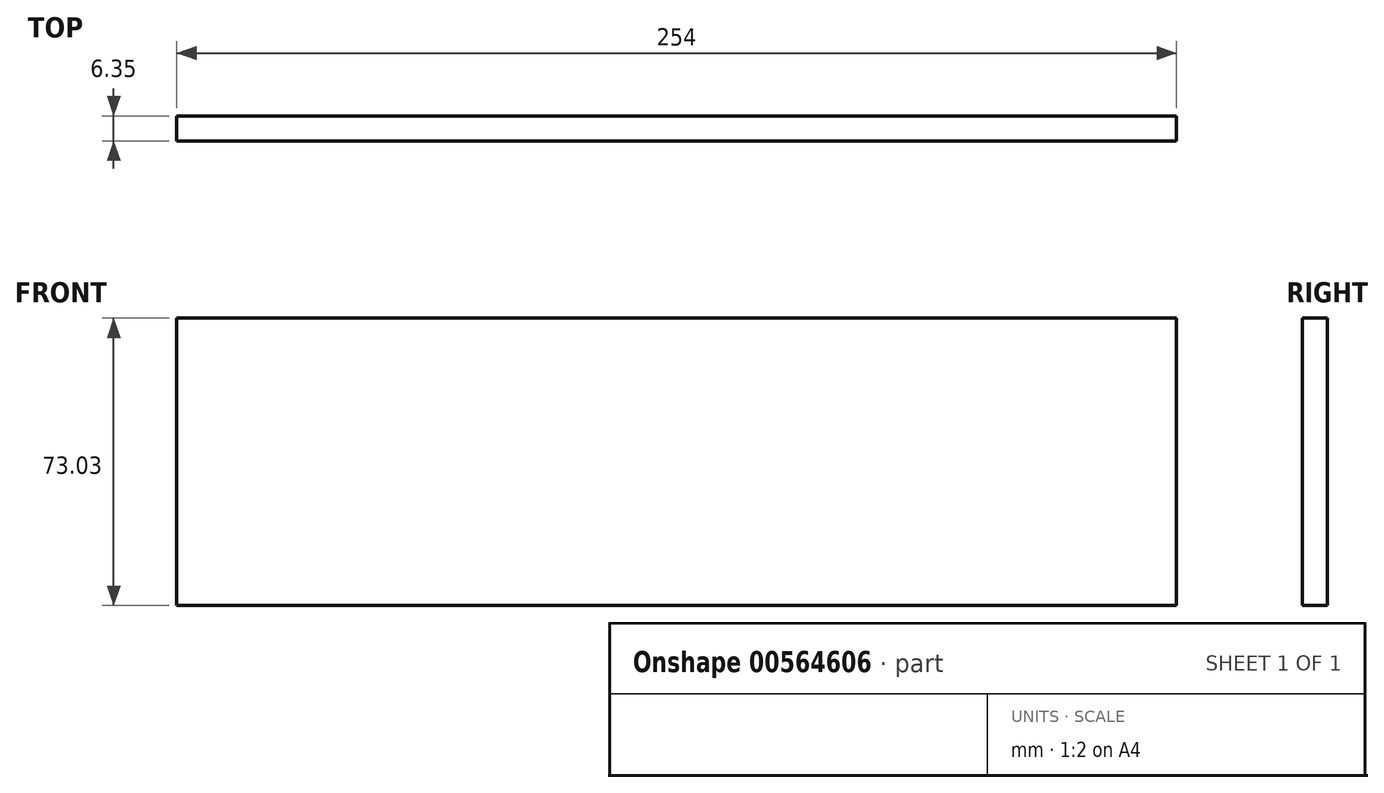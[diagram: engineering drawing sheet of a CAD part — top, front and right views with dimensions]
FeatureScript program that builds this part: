
annotation { "Feature Type Name" : "Feature", "Feature Type Description" : "" }
export const myFeature = defineFeature(function(context is Context, id is Id, definition is map)
    precondition{}
    {
        {
            var Q0;
            Q0=qCreatedBy(makeId("Front.planeOp"),FACE);
            var sketch = newSketch(context, id + "F0", { "sketchPlane" : qUnion([Q0])});
            skLineSegment(sketch, "E0.bottom", {"start": v(-88.8, 33.85) * mm, "end": v(165.2, 33.85) * mm});
            skLineSegment(sketch, "E0.top", {"start": v(-88.8, -39.18) * mm, "end": v(165.2, -39.18) * mm});
            skLineSegment(sketch, "E0.left", {"start": v(-88.8, 33.85) * mm, "end": v(-88.8, -39.18) * mm});
            skLineSegment(sketch, "E0.right", {"start": v(165.2, 33.85) * mm, "end": v(165.2, -39.18) * mm});
            skSolve(sketch);
        }
        {
            var Q0;
            Q0=makeQuery(id+"F0.imprint","IMPRINT",FACE,{"disambiguationData":[TD([[makeQuery(id+"F0.imprint","IMPRINT",EDGE,{"derivedFrom":sQuery(id+"F0.wireOp",EDGE,"E0.bottom")}),-1.0]])]});
            extrude(context, id + "F1", {"entities" : qUnion([Q0]), "depth" : 6.35 * mm, "offsetDistance" : 25.4 * mm});
        }
    });
